# Revit family: BLAUBERG-KOMFORT_Roto_EC_S2 200_SE2 200
name_source: partatom
category: Mechanical Equipment
units: mm (PartAtom-declared; Revit-internal decimal feet)

## family parameters
Always vertical = Yes
Classification = None
Cut with Voids When Loaded = No
OmniClass Number = 23.75.35.14
OmniClass Title = Air Handling Units
Part Type = Normal
Room Calculation Point = No
Round Connector Dimension = Use Diameter
Shared = No
Work Plane-Based = No

## types (2) — shared parameters
B = 348 mm  [stored 1.14173 ft]
B1 = 95 mm
B2 = 95 mm
B4 = 330 mm
Casing Material = Painted Steel White
D = 125 mm  [stored 0.410105 ft]
Description = Air Handling Unit
Duct Connection Diameter = 125 mm  [stored 0.410105 ft]
ElBoxA = 125 mm  [stored 0.410105 ft]
ElBoxB = 70 mm  [stored 0.229659 ft]
ElConA = 105 mm  [stored 0.344488 ft]
ElConB = 75 mm
Extract Air Filter = G4
Family Version = 1.0
Front Maintenance Zone Height = 1000 mm  [stored 3.28084 ft]
Front Maintenance Zone Length = 600 mm  [stored 1.9685 ft]
Front Maintenance Zone Width = 700 mm  [stored 2.29659 ft]
H = 700 mm  [stored 2.29659 ft]
HDuctCon = 50 mm  [stored 0.164042 ft]
Heat Exchanger Material = aluminium
Heat Exchanger Type = rotary
Heat recovery efficiency (%) = 75..92
L = 600 mm  [stored 1.9685 ft]
L1 = 95 mm
L2 = 264 mm  [stored 0.866142 ft]
L3 = 144 mm  [stored 0.472441 ft]
L4 = 268 mm  [stored 0.879265 ft]
Load Classification = HVAC
Maintenance Zone Material = Maintenance Zone
Manufacturer = Blauberg
Maximum Air Flow = 270 m³/h
Maximum Unit Current Without Electric Heater = 1 A
Maximum Unit Power Without Electric Heater = 118 W
Metal Material = Metal Zinc
Number of Poles = 1
Plastic Material = Polypropylene Black
Power Factor = 1
RPM (min-1) = 1800
SEC Class = A
ServiceDoorB = 19 mm
Sound Pressure Level at 3 m (dBA) = 28
Supply Air Filter = G4, F7
Transported Air Temperature (°C) = -25…+40
URL = https://blaubergventilatoren.de
Voltage = 230 V
dBFeets = 65 mm  [stored 0.213255 ft]
dLFeets = 25 mm  [stored 0.082021 ft]

## per-type parameters (varying)
| type | Current | Heater power | Maximum Unit Current With Electric Heater | Power | Type Comments | Weight |
| KOMFORT Roto EC S2 200 S21 | 1 A | 0 W | 1 A | 118 W | Air Handling Unit KOMFORT Roto EC S2 200 S21 | 47.00 kg |
| KOMFORT Roto EC S2E 200 S21 | 4 A | 700 W | 4 A | 818 W | Air Handling Unit KOMFORT Roto EC S2E 200 S21 | 48.00 kg |

note: column(s) folded — value = type name in every type: Model

note: [stored X ft] marks values corroborated as IEEE doubles in the binary element streams (Revit-internal decimal feet)

## geometry (parser evidence)
native form markers: Sweep x9
no freeform markers — native parametric forms only
